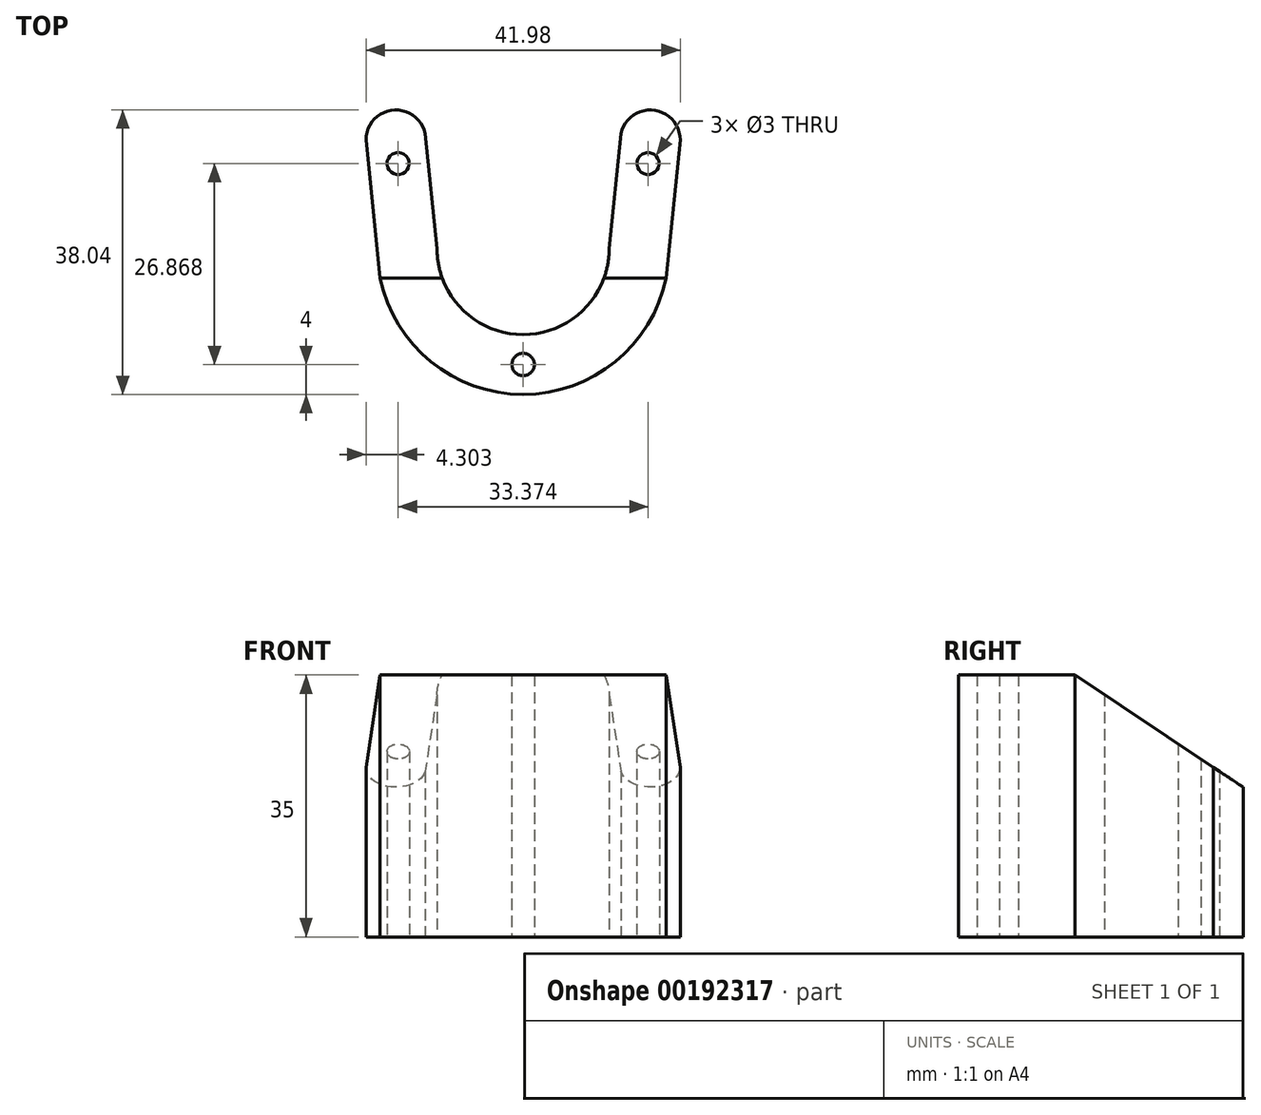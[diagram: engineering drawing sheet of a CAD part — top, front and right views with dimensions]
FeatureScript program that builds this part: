
annotation { "Feature Type Name" : "Feature", "Feature Type Description" : "" }
export const myFeature = defineFeature(function(context is Context, id is Id, definition is map)
    precondition{}
    {
        {
            var Q0;
            Q0=qCreatedBy(makeId("Top.planeOp"),FACE);
            var sketch = newSketch(context, id + "F0", { "sketchPlane" : qUnion([Q0])});
            skCircle(sketch, "E0", {"center": v(0, 0) * mm, "radius": 11.5 * mm});
            skLineSegment(sketch, "E1.bottom", {"start": v(23.5, -19.5) * mm, "end": v(-23.5, -19.5) * mm});
            skLineSegment(sketch, "E1.top", {"start": v(23.5, 19.5) * mm, "end": v(-23.5, 19.5) * mm});
            skLineSegment(sketch, "E1.left", {"start": v(23.5, -19.5) * mm, "end": v(23.5, 19.5) * mm});
            skLineSegment(sketch, "E1.right", {"start": v(-23.5, -19.5) * mm, "end": v(-23.5, 19.5) * mm});
            skLineSegment(sketch, "E2", {"start": v(-11.5, 0) * mm, "end": v(-13.5, 19.5) * mm});
            skLineSegment(sketch, "E3", {"start": v(-21.5, 19.5) * mm, "end": v(-17.5, -19.5) * mm});
            skArc(sketch, "E4", {"start": v(-19.1, -3.96) * mm, "mid": v(0, -19.5) * mm, "end": v(19.1, -3.96) * mm});
            skCircle(sketch, "E5", {"center": v(0, -15.5) * mm, "radius": 1.5 * mm});
            skArc(sketch, "E6", {"start": v(-13, 14.54) * mm, "mid": v(-17, 18.54) * mm, "end": v(-21, 14.54) * mm});
            skLineSegment(sketch, "E7", {"start": v(-23.5, 11.31) * mm, "end": v(23.5, 11.69) * mm, "construction": true});
            skCircle(sketch, "E8", {"center": v(-16.69, 11.37) * mm, "radius": 1.5 * mm});
            skLineSegment(sketch, "E9", {"start": v(0, 19.5) * mm, "end": v(0, -19.5) * mm, "construction": true});
            skCircle(sketch, "E10.MirrorC", {"center": v(16.69, 11.37) * mm, "radius": 1.5 * mm});
            skLineSegment(sketch, "E11.MirrorCS", {"start": v(11.5, 0) * mm, "end": v(13.5, 19.5) * mm});
            skLineSegment(sketch, "E12.MirrorCS", {"start": v(21.5, 19.5) * mm, "end": v(17.5, -19.5) * mm});
            skArc(sketch, "E13.MirrorCS", {"start": v(13, 14.54) * mm, "mid": v(17, 18.54) * mm, "end": v(21, 14.54) * mm});
            skArc(sketch, "E14.trimOffspring", {"start": v(13, 14.54) * mm, "mid": v(0, 19.5) * mm, "end": v(-13, 14.54) * mm});
            skSolve(sketch);
        }
        {
            var Q0;
            Q0=makeQuery(id+"F0.imprint","IMPRINT",FACE,{"disambiguationData":[TD([[makeQuery(id+"F0.imprint","IMPRINT",EDGE,{"derivedFrom":sQuery(id+"F0.wireOp",EDGE,"E5")}),-1.0]])]});
            extrude(context, id + "F1", {"entities" : qUnion([Q0]), "depth" : 35 * mm});
        }
        {
            var Q0;
            Q0=qCreatedBy(makeId("Right.planeOp"),FACE);
            var sketch = newSketch(context, id + "F2", { "sketchPlane" : qUnion([Q0])});
            skLineSegment(sketch, "E15.0", {"start": v(-3.96, 35) * mm, "end": v(-19.5, 35) * mm});
            skLineSegment(sketch, "E15.1.0", {"start": v(-3.96, 0) * mm, "end": v(-19.5, 0) * mm});
            skLineSegment(sketch, "E15.1.2", {"start": v(-3.96, 35) * mm, "end": v(-19.5, 35) * mm});
            skLineSegment(sketch, "E15.2.0", {"start": v(-3.96, 0) * mm, "end": v(14.54, 0) * mm});
            skLineSegment(sketch, "E15.2.2", {"start": v(14.54, 35) * mm, "end": v(-3.96, 35) * mm});
            skLineSegment(sketch, "E15.3.0", {"start": v(14.54, 0) * mm, "end": v(18.54, 0) * mm});
            skLineSegment(sketch, "E15.3.2", {"start": v(18.54, 35) * mm, "end": v(14.54, 35) * mm});
            skLineSegment(sketch, "E16", {"start": v(-2.06, 20) * mm, "end": v(16.58, 20) * mm, "construction": true});
            skLineSegment(sketch, "E17", {"start": v(-3.96, 35) * mm, "end": v(18.54, 20) * mm});
            skLineSegment(sketch, "E18", {"start": v(18.54, 35) * mm, "end": v(18.54, 20) * mm});
            skSolve(sketch);
        }
        {
            var Q0;
            Q0=makeQuery(id+"F2.imprint","IMPRINT",FACE,{"disambiguationData":[TD([[makeQuery(id+"F2.imprint","IMPRINT",EDGE,{"derivedFrom":sQuery(id+"F2.wireOp",EDGE,"E15.2.2")}),1.0]])]});
            extrude(context, id + "F3", {"entities" : qUnion([Q0]), "operationType" : NewBodyOperationType.REMOVE, "endBound" : BoundingType.THROUGH_ALL, "depth" : 25 * mm, "hasSecondDirection" : true, "secondDirectionBound" : SecondDirectionBoundingType.THROUGH_ALL, "secondDirectionOppositeDirection" : true, "secondDirectionDepth" : 25 * mm});
        }
    });
